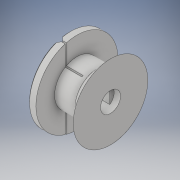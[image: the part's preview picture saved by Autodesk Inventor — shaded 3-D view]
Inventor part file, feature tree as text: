
AUTODESK INVENTOR PART (.ipt)
format: ipt  version: 2019 (Build 230136000, 136)  size: 182,272 bytes
history: native  units: mm
features: sketch x4, extrude x4, chamfer x2, projected_geometry x2, revolve x1
ambient origin geometry x8: Origin, YZ Plane, XZ Plane, XY Plane, X Axis, Y Axis, Z Axis, Center Point
bodies: Volumenkörper1 (feature_tree)
feature tree (13):
  revolve  "Umdrehung1"
  sketch  "Skizze3"  dims[d2=2.0mm d3=5.0mm]
  extrude  "Extrusion1"  Depth=6.0mm
  extrude  "Extrusion2"  Depth=5.0mm
  extrude  "Extrusion3"  Depth=4.0mm
  chamfer  "Fase1"  Distance=1.7mm
  chamfer  "Fase2"  Distance=0.31mm
  extrude  "Extrusion4"  Depth=10.0mm
  sketch  "Skizze1"  dims[d0=11.0mm d1=6.0mm]
  projected_geometry  "Projizierte Kontur1"
  sketch  "Skizze4"  dims[d5=5.5mm d6=4.0mm]
  projected_geometry  "Projizierte Kontur2"
  sketch  "Skizze5"  dims[d7=90.0deg d8=5.35mm d9=1.5mm d10=1.5mm d11=8.5mm d12=0.0mm d13=1.7mm d14=0.0mm d15=0.31mm d16=2.84mm d17=6.5mm d18=0.0mm d19=1.0mm d20=2.0mm d21=45.0deg d22=0.3mm d23=2.0mm d24=45.0deg d25=3.6mm d26=4.5mm d27=10.0mm d28=0.0mm]
